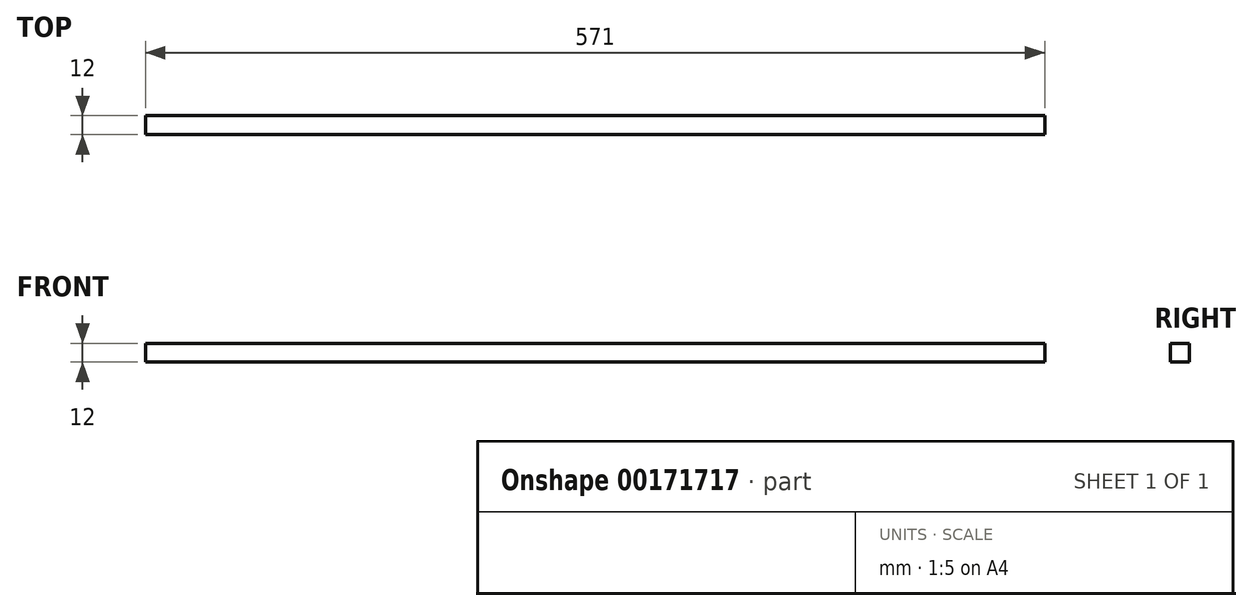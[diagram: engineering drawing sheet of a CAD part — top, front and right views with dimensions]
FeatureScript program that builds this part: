
annotation { "Feature Type Name" : "Feature", "Feature Type Description" : "" }
export const myFeature = defineFeature(function(context is Context, id is Id, definition is map)
    precondition{}
    {
        {
            var Q0;
            Q0=qCreatedBy(makeId("Right.planeOp"),FACE);
            var sketch = newSketch(context, id + "F0", { "sketchPlane" : qUnion([Q0])});
            skLineSegment(sketch, "E0.bottom", {"start": v(-6, 6) * mm, "end": v(6, 6) * mm});
            skLineSegment(sketch, "E0.top", {"start": v(-6, -6) * mm, "end": v(6, -6) * mm});
            skLineSegment(sketch, "E0.left", {"start": v(-6, 6) * mm, "end": v(-6, -6) * mm});
            skLineSegment(sketch, "E0.right", {"start": v(6, 6) * mm, "end": v(6, -6) * mm});
            skPoint(sketch, "E0.middle", {"position": v(0, 0) * mm});
            skSolve(sketch);
        }
        {
            var Q0;
            Q0=makeQuery(id+"F0.imprint","IMPRINT",FACE,{"disambiguationData":[TD([[makeQuery(id+"F0.imprint","IMPRINT",EDGE,{"derivedFrom":sQuery(id+"F0.wireOp",EDGE,"E0.bottom")}),-1.0]])]});
            extrude(context, id + "F1", {"entities" : qUnion([Q0]), "depth" : 571 * mm});
        }
    });
